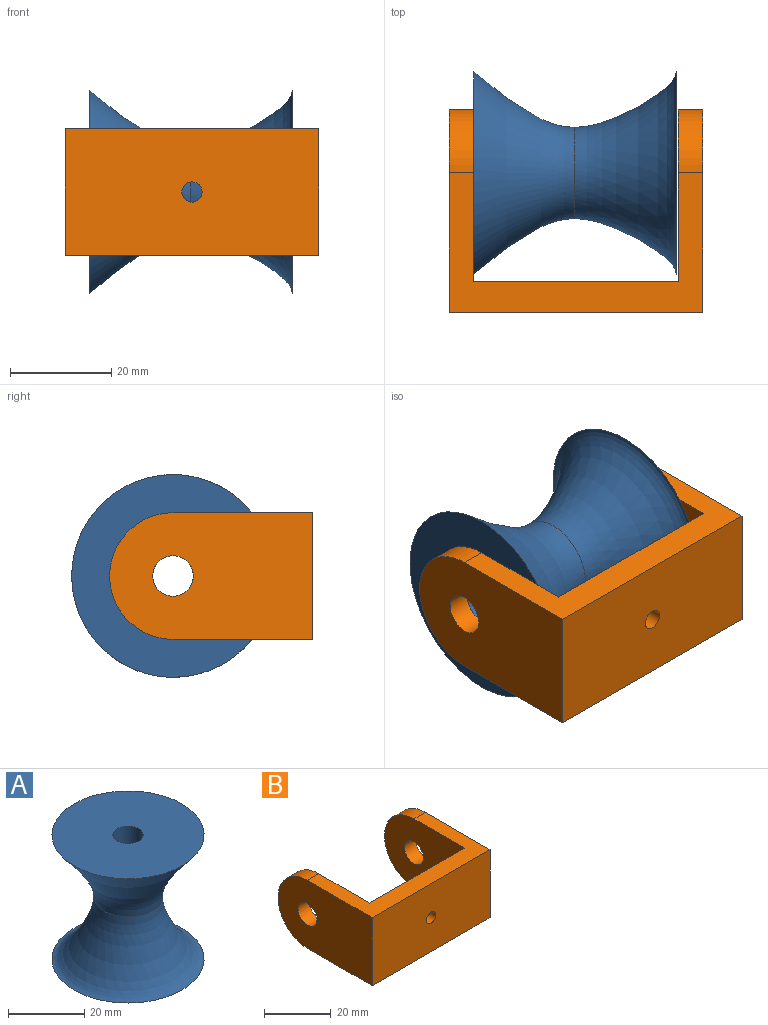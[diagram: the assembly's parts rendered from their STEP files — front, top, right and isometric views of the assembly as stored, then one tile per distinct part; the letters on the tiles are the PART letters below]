
ASSEMBLY  parts=2 mates=1
PART A: 5 faces, bbox 40x40x40 mm
  f0: plane 40x40mm, normal (0,0,-1), area 1206.3mm2, adj f1,f4
  f1: bspline ~40x40mm, area 1945.3mm2, adj f0,f3
  f2: plane 40x40mm, normal (0,0,1), area 1206.3mm2, adj f3,f4
  f3: bspline ~40x40mm, area 1958.9mm2, adj f1,f2
  f4: cylinder r=4mm len=40mm, axis (0,0,-1), area 1005.3mm2, adj f0,f2
PART B: 16 faces, bbox 50x40x25 mm
  f0: plane 40.4x25mm, normal (0,1,0), area 959.7mm2, adj f1,f5,f6,f7,f15
  f1: plane 34x25mm, normal (1,0,0), area 732.5mm2, adj f0,f6,f7,f10,f11,f13
  f2: plane 40x25mm, normal (-1,0,0), area 882.5mm2, adj f3,f6,f7,f10,f11,f13
  f3: plane 50x25mm, normal (0,-1,0), area 1237.4mm2, adj f2,f4,f6,f7,f14
  f4: plane 40x25mm, normal (1,0,0), area 882.5mm2, adj f3,f6,f7,f8,f9,f12
  f5: plane 34x25mm, normal (-1,0,0), area 732.5mm2, adj f0,f6,f7,f8,f9,f12
  f6: plane 50x27.49mm, normal (0,0,1), area 506.3mm2, adj f0,f1,f2,f3,f4,f5,f8,f10
  f7: plane 50x27.49mm, normal (0,0,-1), area 506.3mm2, adj f0,f1,f2,f3,f4,f5,f9,f11
  f8: cylinder r=12.51mm len=12.51mm, axis (1,0,0), area 94.3mm2, adj f4,f5,f6,f9
  f9: cylinder r=12.51mm len=12.51mm, axis (-1,0,0), area 94.3mm2, adj f4,f5,f7,f8
  f10: cylinder r=12.51mm len=12.51mm, axis (1,0,0), area 94.3mm2, adj f1,f2,f6,f11
  f11: cylinder r=12.51mm len=12.51mm, axis (-1,0,0), area 94.3mm2, adj f1,f2,f7,f10
  f12: cylinder r=4mm len=8mm, axis (-1,0,0), area 120.6mm2, adj f4,f5
  f13: cylinder r=4mm len=8mm, axis (-1,0,0), area 120.6mm2, adj f1,f2
  f14: cylinder r=2mm len=4mm, axis (0,1,0), area 50.3mm2, adj f3,f15
  f15: cone r=2mm half-angle=45deg, axis (0,1,0), area 53.3mm2, adj f0,f14
PLACE A rot(axis=(0.71,0,-0.71),180deg) t=(19.8,27.49,0.01)mm
PLACE B at identity
MATE cylindrical A.f4 <-> B.f9  axis (1,0,0) through (-20.2,27.49,0.01)mm
